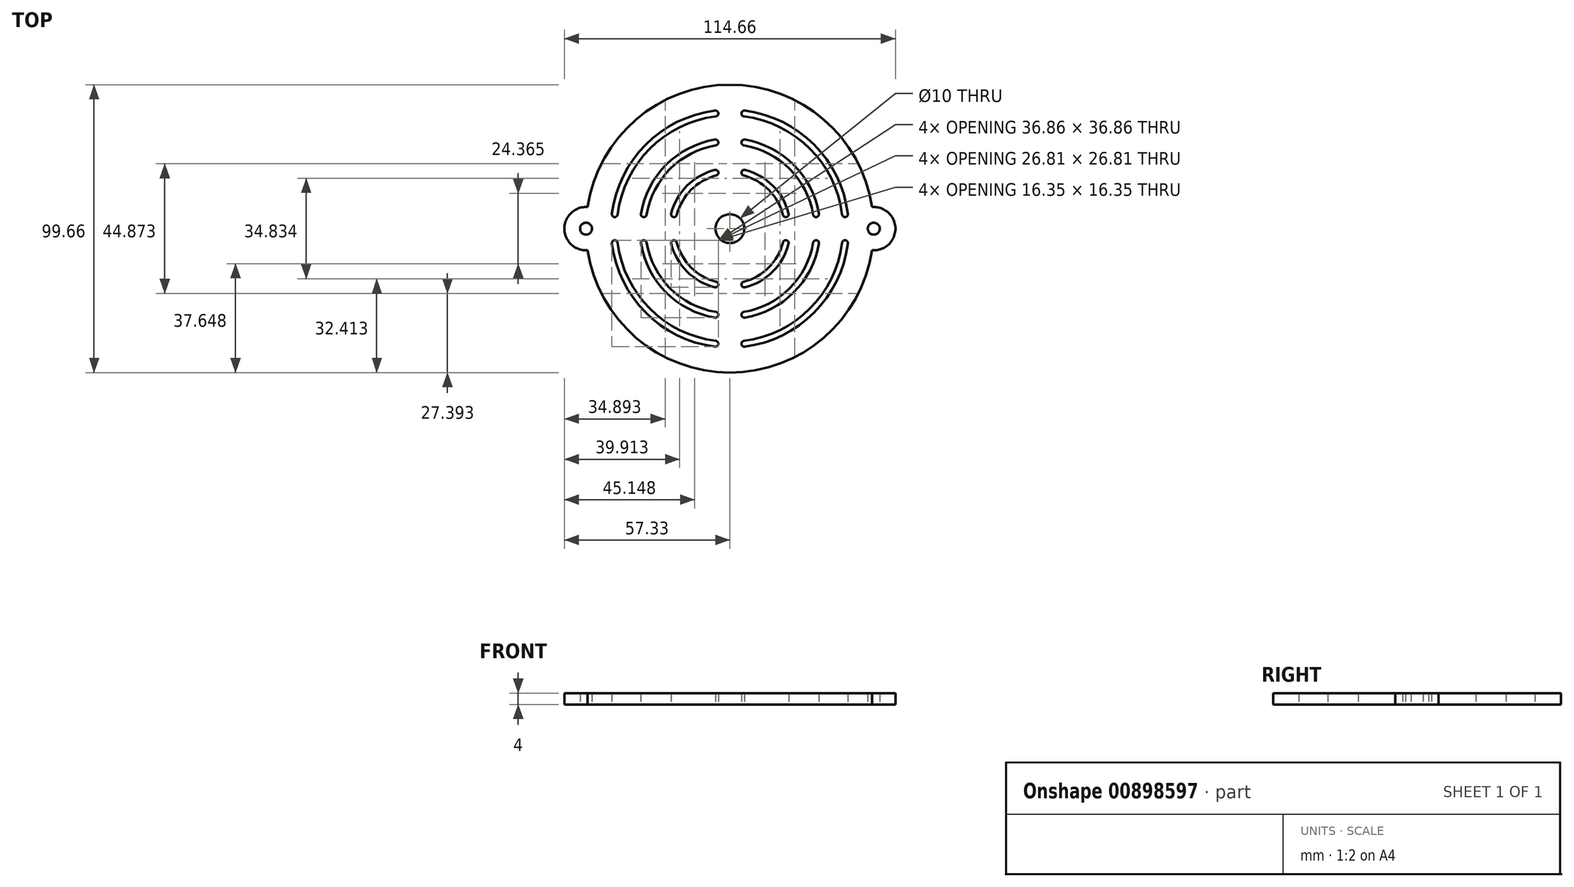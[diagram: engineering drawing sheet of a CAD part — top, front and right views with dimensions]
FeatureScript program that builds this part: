
annotation { "Feature Type Name" : "Feature", "Feature Type Description" : "" }
export const myFeature = defineFeature(function(context is Context, id is Id, definition is map)
    precondition{}
    {
        {
            var Q0;
            Q0=qCreatedBy(makeId("Top.planeOp"),FACE);
            var sketch = newSketch(context, id + "F0", { "sketchPlane" : qUnion([Q0])});
            skCircle(sketch, "E0", {"center": v(-49.83, 0) * mm, "radius": 2.08 * mm});
            skCircle(sketch, "E1", {"center": v(49.83, 0) * mm, "radius": 2.08 * mm});
            skLineSegment(sketch, "E2", {"start": v(0, 50.77) * mm, "end": v(0, -49.23) * mm, "construction": true});
            skArc(sketch, "E3", {"start": v(-49.27, 7.48) * mm, "mid": v(-57.33, 0) * mm, "end": v(-49.27, -7.48) * mm});
            skArc(sketch, "E4", {"start": v(49.27, -7.48) * mm, "mid": v(57.33, 0) * mm, "end": v(49.27, 7.48) * mm});
            skArc(sketch, "E5.trimOffspring", {"start": v(-49.27, -7.48) * mm, "mid": v(0, -49.83) * mm, "end": v(49.27, -7.48) * mm});
            skArc(sketch, "E6.trimOffspring", {"start": v(49.27, 7.48) * mm, "mid": v(0, 49.83) * mm, "end": v(-49.27, 7.48) * mm});
            skCircle(sketch, "E7", {"center": v(0, 0) * mm, "radius": 5 * mm});
            skArc(sketch, "E8.0.startCap", {"start": v(-5.12, 40.87) * mm, "mid": v(-4, 40) * mm, "end": v(-4.88, 38.88) * mm});
            skArc(sketch, "E8.0.endCap", {"start": v(-38.88, 4.88) * mm, "mid": v(-40, 4) * mm, "end": v(-40.87, 5.12) * mm});
            skArc(sketch, "E8.0.left", {"start": v(-4.88, 38.88) * mm, "mid": v(-27.7, 27.7) * mm, "end": v(-38.88, 4.88) * mm});
            skArc(sketch, "E8.0.right", {"start": v(-5.12, 40.87) * mm, "mid": v(-29.12, 29.12) * mm, "end": v(-40.87, 5.12) * mm});
            skArc(sketch, "E8.1.startCap", {"start": v(-5.17, 30.82) * mm, "mid": v(-4.01, 30) * mm, "end": v(-4.83, 28.85) * mm});
            skArc(sketch, "E8.1.endCap", {"start": v(-28.85, 4.83) * mm, "mid": v(-30, 4.01) * mm, "end": v(-30.82, 5.17) * mm});
            skArc(sketch, "E8.1.left", {"start": v(-4.83, 28.85) * mm, "mid": v(-20.68, 20.68) * mm, "end": v(-28.85, 4.83) * mm});
            skArc(sketch, "E8.1.right", {"start": v(-5.17, 30.82) * mm, "mid": v(-22.1, 22.1) * mm, "end": v(-30.82, 5.17) * mm});
            skArc(sketch, "E8.2.startCap", {"start": v(-5.25, 20.33) * mm, "mid": v(-4.03, 19.61) * mm, "end": v(-4.75, 18.4) * mm});
            skArc(sketch, "E8.2.endCap", {"start": v(-18.4, 4.75) * mm, "mid": v(-19.61, 4.03) * mm, "end": v(-20.33, 5.25) * mm});
            skArc(sketch, "E8.2.left", {"start": v(-4.75, 18.4) * mm, "mid": v(-13.44, 13.44) * mm, "end": v(-18.4, 4.75) * mm});
            skArc(sketch, "E8.2.right", {"start": v(-5.25, 20.33) * mm, "mid": v(-14.85, 14.85) * mm, "end": v(-20.33, 5.25) * mm});
            skArc(sketch, "E9.1.0", {"start": v(-40.87, -5.12) * mm, "mid": v(-29.12, -29.12) * mm, "end": v(-5.12, -40.87) * mm});
            skArc(sketch, "E9.1.1", {"start": v(-18.4, -4.75) * mm, "mid": v(-13.44, -13.44) * mm, "end": v(-4.75, -18.4) * mm});
            skArc(sketch, "E9.1.2", {"start": v(-38.88, -4.88) * mm, "mid": v(-27.7, -27.7) * mm, "end": v(-4.88, -38.88) * mm});
            skArc(sketch, "E9.1.3", {"start": v(-30.82, -5.17) * mm, "mid": v(-22.1, -22.1) * mm, "end": v(-5.17, -30.82) * mm});
            skArc(sketch, "E9.1.4", {"start": v(-28.85, -4.83) * mm, "mid": v(-20.68, -20.68) * mm, "end": v(-4.83, -28.85) * mm});
            skArc(sketch, "E9.1.5", {"start": v(-20.33, -5.25) * mm, "mid": v(-14.85, -14.85) * mm, "end": v(-5.25, -20.33) * mm});
            skArc(sketch, "E9.1.6", {"start": v(-20.33, -5.25) * mm, "mid": v(-19.61, -4.03) * mm, "end": v(-18.4, -4.75) * mm});
            skArc(sketch, "E9.1.7", {"start": v(-4.88, -38.88) * mm, "mid": v(-4, -40) * mm, "end": v(-5.12, -40.87) * mm});
            skArc(sketch, "E9.1.8", {"start": v(-30.82, -5.17) * mm, "mid": v(-30, -4.01) * mm, "end": v(-28.85, -4.83) * mm});
            skArc(sketch, "E9.1.9", {"start": v(-40.87, -5.12) * mm, "mid": v(-40, -4) * mm, "end": v(-38.88, -4.88) * mm});
            skArc(sketch, "E9.1.10", {"start": v(-4.75, -18.4) * mm, "mid": v(-4.03, -19.61) * mm, "end": v(-5.25, -20.33) * mm});
            skArc(sketch, "E9.1.11", {"start": v(-4.83, -28.85) * mm, "mid": v(-4.01, -30) * mm, "end": v(-5.17, -30.82) * mm});
            skArc(sketch, "E9.2.0", {"start": v(5.12, -40.87) * mm, "mid": v(29.12, -29.12) * mm, "end": v(40.87, -5.12) * mm});
            skArc(sketch, "E9.2.1", {"start": v(4.75, -18.4) * mm, "mid": v(13.44, -13.44) * mm, "end": v(18.4, -4.75) * mm});
            skArc(sketch, "E9.2.2", {"start": v(4.88, -38.88) * mm, "mid": v(27.7, -27.7) * mm, "end": v(38.88, -4.88) * mm});
            skArc(sketch, "E9.2.3", {"start": v(5.17, -30.82) * mm, "mid": v(22.1, -22.1) * mm, "end": v(30.82, -5.17) * mm});
            skArc(sketch, "E9.2.4", {"start": v(4.83, -28.85) * mm, "mid": v(20.68, -20.68) * mm, "end": v(28.85, -4.83) * mm});
            skArc(sketch, "E9.2.5", {"start": v(5.25, -20.33) * mm, "mid": v(14.85, -14.85) * mm, "end": v(20.33, -5.25) * mm});
            skArc(sketch, "E9.2.6", {"start": v(5.25, -20.33) * mm, "mid": v(4.03, -19.61) * mm, "end": v(4.75, -18.4) * mm});
            skArc(sketch, "E9.2.7", {"start": v(38.88, -4.88) * mm, "mid": v(40, -4) * mm, "end": v(40.87, -5.12) * mm});
            skArc(sketch, "E9.2.8", {"start": v(5.17, -30.82) * mm, "mid": v(4.01, -30) * mm, "end": v(4.83, -28.85) * mm});
            skArc(sketch, "E9.2.9", {"start": v(5.12, -40.87) * mm, "mid": v(4, -40) * mm, "end": v(4.88, -38.88) * mm});
            skArc(sketch, "E9.2.10", {"start": v(18.4, -4.75) * mm, "mid": v(19.61, -4.03) * mm, "end": v(20.33, -5.25) * mm});
            skArc(sketch, "E9.2.11", {"start": v(28.85, -4.83) * mm, "mid": v(30, -4.01) * mm, "end": v(30.82, -5.17) * mm});
            skArc(sketch, "E9.3.0", {"start": v(40.87, 5.12) * mm, "mid": v(29.12, 29.12) * mm, "end": v(5.12, 40.87) * mm});
            skArc(sketch, "E9.3.1", {"start": v(18.4, 4.75) * mm, "mid": v(13.44, 13.44) * mm, "end": v(4.75, 18.4) * mm});
            skArc(sketch, "E9.3.2", {"start": v(38.88, 4.88) * mm, "mid": v(27.7, 27.7) * mm, "end": v(4.88, 38.88) * mm});
            skArc(sketch, "E9.3.3", {"start": v(30.82, 5.17) * mm, "mid": v(22.1, 22.1) * mm, "end": v(5.17, 30.82) * mm});
            skArc(sketch, "E9.3.4", {"start": v(28.85, 4.83) * mm, "mid": v(20.68, 20.68) * mm, "end": v(4.83, 28.85) * mm});
            skArc(sketch, "E9.3.5", {"start": v(20.33, 5.25) * mm, "mid": v(14.85, 14.85) * mm, "end": v(5.25, 20.33) * mm});
            skArc(sketch, "E9.3.6", {"start": v(20.33, 5.25) * mm, "mid": v(19.61, 4.03) * mm, "end": v(18.4, 4.75) * mm});
            skArc(sketch, "E9.3.7", {"start": v(4.88, 38.88) * mm, "mid": v(4, 40) * mm, "end": v(5.12, 40.87) * mm});
            skArc(sketch, "E9.3.8", {"start": v(30.82, 5.17) * mm, "mid": v(30, 4.01) * mm, "end": v(28.85, 4.83) * mm});
            skArc(sketch, "E9.3.9", {"start": v(40.87, 5.12) * mm, "mid": v(40, 4) * mm, "end": v(38.88, 4.88) * mm});
            skArc(sketch, "E9.3.10", {"start": v(4.75, 18.4) * mm, "mid": v(4.03, 19.61) * mm, "end": v(5.25, 20.33) * mm});
            skArc(sketch, "E9.3.11", {"start": v(4.83, 28.85) * mm, "mid": v(4.01, 30) * mm, "end": v(5.17, 30.82) * mm});
            skSolve(sketch);
        }
        {
            var Q0;
            Q0=qSketchRegion(id+"F0",true);
            extrude(context, id + "F1", {"entities" : qUnion([Q0]), "depth" : 4 * mm});
        }
    });
